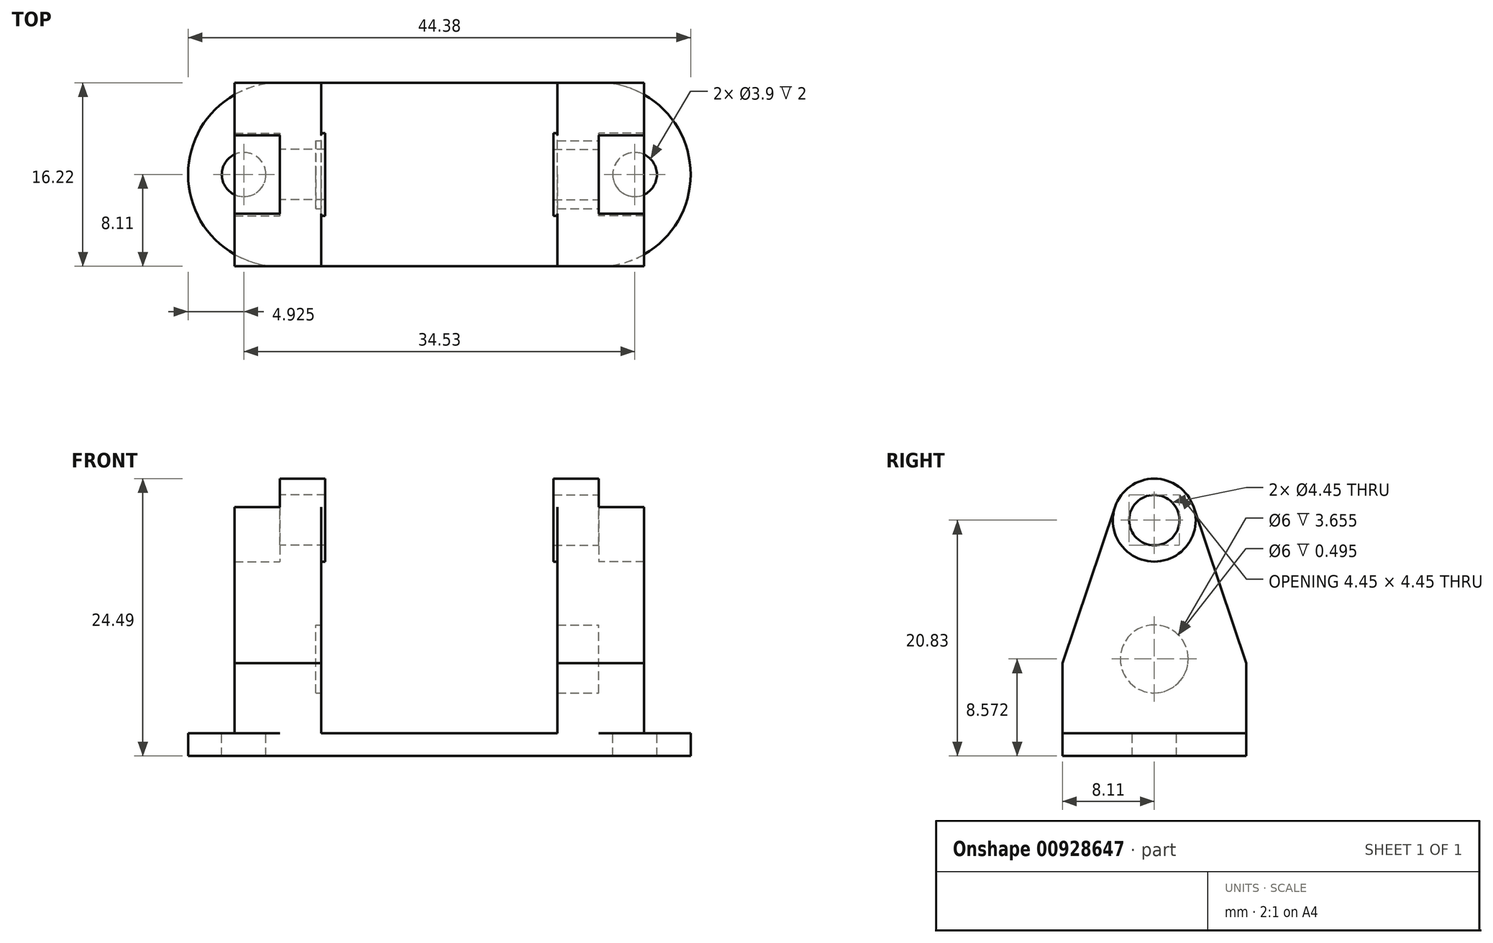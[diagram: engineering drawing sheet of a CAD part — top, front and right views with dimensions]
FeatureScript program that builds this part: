
annotation { "Feature Type Name" : "Feature", "Feature Type Description" : "" }
export const myFeature = defineFeature(function(context is Context, id is Id, definition is map)
    precondition{}
    {
        {
            var Q0;
            Q0=qCreatedBy(makeId("Top.planeOp"),FACE);
            var sketch = newSketch(context, id + "F0", { "sketchPlane" : qUnion([Q0])});
            skLineSegment(sketch, "E0.bottom", {"start": v(0, -8.1) * mm, "end": v(-14.08, -8.11) * mm});
            skLineSegment(sketch, "E0.top", {"start": v(0, 8.11) * mm, "end": v(-14.08, 8.1) * mm});
            skPoint(sketch, "E0.middle", {"position": v(0, 0) * mm});
            skPoint(sketch, "E1.center.orphan", {"position": v(-14.08, 0) * mm});
            skArc(sketch, "E2", {"start": v(-14.08, -8.11) * mm, "mid": v(-22.2, 0) * mm, "end": v(-14.08, 8.1) * mm});
            skLineSegment(sketch, "E3", {"start": v(0, 0) * mm, "end": v(0, -8.1) * mm});
            skLineSegment(sketch, "E4", {"start": v(0, -8.1) * mm, "end": v(0, 8.1) * mm});
            skPoint(sketch, "E5.center.orphan", {"position": v(14.08, 0) * mm});
            skPoint(sketch, "E5.end.orphan", {"position": v(14.08, -8.1) * mm});
            skPoint(sketch, "E6.orphan", {"position": v(14.08, 8.11) * mm});
            skSolve(sketch);
        }
        {
            var Q0;
            Q0=makeQuery(id+"F0.imprint","IMPRINT",FACE,{"disambiguationData":[TD([[makeQuery(id+"F0.imprint","IMPRINT",EDGE,{"derivedFrom":sQuery(id+"F0.wireOp",EDGE,"E0.bottom")}),-1.0]])]});
            extrude(context, id + "F1", {"entities" : qUnion([Q0]), "depth" : 2 * mm, "offsetDistance" : 25 * mm});
        }
        {
            var Q0;
            Q0=qCreatedBy(makeId("Right.planeOp"),FACE);
            var sketch = newSketch(context, id + "F2", { "sketchPlane" : qUnion([Q0])});
            skLineSegment(sketch, "E7", {"start": v(-8.11, 2) * mm, "end": v(-8.11, 8.21) * mm});
            skLineSegment(sketch, "E8", {"start": v(-8.11, 8.21) * mm, "end": v(-3.47, 22) * mm});
            skLineSegment(sketch, "E9", {"start": v(3.47, 22) * mm, "end": v(8.1, 8.21) * mm});
            skLineSegment(sketch, "E10", {"start": v(8.1, 8.21) * mm, "end": v(8.1, 2) * mm});
            skLineSegment(sketch, "E11", {"start": v(8.1, 2) * mm, "end": v(-8.1, 2) * mm});
            skPoint(sketch, "E12.end.orphan", {"position": v(0, 20.83) * mm});
            skPoint(sketch, "E12.start.orphan", {"position": v(0, 2) * mm});
            skArc(sketch, "E13", {"start": v(3.47, 22) * mm, "mid": v(0, 24.5) * mm, "end": v(-3.47, 22) * mm});
            skSolve(sketch);
        }
        {
            var Q0;
            Q0=makeQuery(id+"F2.imprint","IMPRINT",FACE,{"disambiguationData":[TD([[makeQuery(id+"F2.imprint","IMPRINT",EDGE,{"derivedFrom":sQuery(id+"F2.wireOp",EDGE,"E7")}),-1.0]])]});
            extrude(context, id + "F3", {"entities" : qUnion([Q0]), "operationType" : NewBodyOperationType.ADD, "oppositeDirection" : true, "depth" : 14.08 * mm, "offsetDistance" : 25 * mm});
        }
        {
            var Q0;
            Q0=makeQuery(id+"F3.opExtrude","CAP_FACE",FACE,{"disambiguationData":[OSD([sQuery(id+"F2.wireOp",EDGE,"E7"),sQuery(id+"F2.wireOp",EDGE,"E8"),sQuery(id+"F2.wireOp",EDGE,"284b882a-70f0-48d0-840a-5051115d6a00"),sQuery(id+"F2.wireOp",EDGE,"E9"),sQuery(id+"F2.wireOp",EDGE,"E10"),sQuery(id+"F2.wireOp",EDGE,"E11")])],"isStart":true});
            extrude(context, id + "F4", {"entities" : qUnion([Q0]), "operationType" : NewBodyOperationType.REMOVE, "oppositeDirection" : true, "depth" : 10.43 * mm, "offsetDistance" : 25 * mm});
        }
        {
            var Q0;
            Q0=makeQuery(id+"F3.opExtrude","CAP_FACE",FACE,{"disambiguationData":[OSD([sQuery(id+"F2.wireOp",EDGE,"E7"),sQuery(id+"F2.wireOp",EDGE,"E8"),sQuery(id+"F2.wireOp",EDGE,"E9"),sQuery(id+"F2.wireOp",EDGE,"E10"),sQuery(id+"F2.wireOp",EDGE,"E11"),sQuery(id+"F2.wireOp",EDGE,"E13")])],"isStart":false});
            var sketch = newSketch(context, id + "F5", { "sketchPlane" : qUnion([Q0])});
            skCircle(sketch, "E14", {"center": v(0, 20.83) * mm, "radius": 3.66 * mm});
            skSolve(sketch);
        }
        {
            var Q0;
            {var subQ0=sQuery(id+"F5.wireOp",EDGE,"E14");Q0=makeQuery(id+"F5.imprint","IMPRINT",FACE,{"disambiguationData":[TD([[makeQuery(id+"F5.imprint","IMPRINT",EDGE,{"disambiguationData":[OD(0.0)],"derivedFrom":subQ0}),-1.0]])]});}
            extrude(context, id + "F6", {"entities" : qUnion([Q0]), "operationType" : NewBodyOperationType.ADD, "depth" : 4 * mm, "offsetDistance" : 25 * mm});
        }
        {
            var Q0;
            Q0=makeQuery(id+"F4.boolean.opBoolean","COPY",FACE,{"derivedFrom":makeQuery(id+"F4.opExtrude","CAP_FACE",FACE,{"disambiguationData":[OSD([sQuery(id+"F2.wireOp",EDGE,"E7"),sQuery(id+"F2.wireOp",EDGE,"E8"),sQuery(id+"F2.wireOp",EDGE,"E9"),sQuery(id+"F2.wireOp",EDGE,"E10"),sQuery(id+"F2.wireOp",EDGE,"E11"),sQuery(id+"F2.wireOp",EDGE,"E13")])],"isStart":false})});
            var sketch = newSketch(context, id + "F7", { "sketchPlane" : qUnion([Q0])});
            skCircle(sketch, "E15", {"center": v(0, 20.83) * mm, "radius": 3.66 * mm});
            skSolve(sketch);
        }
        {
            var Q0;
            {var subQ0=sQuery(id+"F7.wireOp",EDGE,"E15");var subQ1=makeQuery(id+"F7.imprint","INTERSECT",VERTEX,{"derivedFrom":[makeQuery(id+"F4.boolean.opBoolean","COPY",EDGE,{"derivedFrom":makeQuery(id+"F4.opExtrude","CAP_EDGE",EDGE,{"disambiguationData":[OSD([sQuery(id+"F2.wireOp",EDGE,"E8")])],"isStart":false})}),subQ0]});Q0=makeQuery(id+"F7.imprint","IMPRINT",FACE,{"disambiguationData":[TD([[makeQuery(id+"F7.imprint","IMPRINT",EDGE,{"disambiguationData":[TD([[subQ1,1.0]])],"derivedFrom":subQ0}),1.0]])]});}
            extrude(context, id + "F8", {"entities" : qUnion([Q0]), "operationType" : NewBodyOperationType.ADD, "depth" : 0.34 * mm, "offsetDistance" : 25 * mm});
        }
        {
            var Q0;
            Q0=makeQuery(id+"F6.opExtrude","CAP_FACE",FACE,{"disambiguationData":[OSD([sQuery(id+"F5.wireOp",EDGE,"E14")])],"isStart":false});
            var sketch = newSketch(context, id + "F9", { "sketchPlane" : qUnion([Q0])});
            skCircle(sketch, "E16", {"center": v(0, 20.83) * mm, "radius": 2.23 * mm});
            skSolve(sketch);
        }
        {
            var Q0;
            Q0=makeQuery(id+"F9.imprint","IMPRINT",FACE,{"disambiguationData":[TD([[makeQuery(id+"F9.imprint","IMPRINT",EDGE,{"derivedFrom":sQuery(id+"F9.wireOp",EDGE,"E16")}),1.0]])]});
            var Q1;
            Q1=sQuery(id+"F9.wireOp",EDGE,"E16");
            extrude(context, id + "F10", {"entities" : qUnion([Q0]), "operationType" : NewBodyOperationType.REMOVE, "surfaceEntities" : qUnion([Q1]), "oppositeDirection" : true, "depth" : 8 * mm, "offsetDistance" : 25 * mm});
        }
        {
            var Q0;
            {var subQ1=sQuery(id+"F0.wireOp",EDGE,"E0.top");var subQ3=sQuery(id+"F0.wireOp",EDGE,"E2");var subQ4=sQuery(id+"F0.wireOp",EDGE,"E0.bottom");Q0=makeQuery(id+"F3.boolean.opBoolean","SPLIT",FACE,{"disambiguationData":[TD([makeQuery(id+"F1.opExtrude","SWEPT_FACE",FACE,{"disambiguationData":[OSD([subQ3])]})])],"derivedFrom":makeQuery(id+"F1.opExtrude","CAP_FACE",FACE,{"disambiguationData":[OSD([subQ4,subQ1,sQuery(id+"F0.wireOp",EDGE,"E5"),subQ3])],"isStart":false})});}
            var sketch = newSketch(context, id + "F11", { "sketchPlane" : qUnion([Q0])});
            skCircle(sketch, "E17", {"center": v(-17.27, 0) * mm, "radius": 1.95 * mm});
            skSolve(sketch);
        }
        {
            var Q0;
            Q0=makeQuery(id+"F11.imprint","IMPRINT",FACE,{"disambiguationData":[TD([[makeQuery(id+"F11.imprint","IMPRINT",EDGE,{"derivedFrom":sQuery(id+"F11.wireOp",EDGE,"E17")}),1.0]])]});
            extrude(context, id + "F12", {"entities" : qUnion([Q0]), "operationType" : NewBodyOperationType.REMOVE, "oppositeDirection" : true, "depth" : 2 * mm, "offsetDistance" : 25 * mm});
        }
        {
            var Q0;
            Q0 = qSketchRegion(id + "F0", true);
            var sketch = newSketch(context, id + "F13", { "sketchPlane" : qUnion([Q0])});
            skLineSegment(sketch, "E18.bottom", {"start": v(-10.43, -8.1) * mm, "end": v(0, -8.1) * mm});
            skLineSegment(sketch, "E18.top", {"start": v(-10.43, 8.11) * mm, "end": v(0, 8.11) * mm});
            skLineSegment(sketch, "E18.left", {"start": v(-10.43, -8.1) * mm, "end": v(-10.43, 8.11) * mm});
            skLineSegment(sketch, "E18.right", {"start": v(0, -8.1) * mm, "end": v(0, 8.11) * mm});
            skSolve(sketch);
        }
        {
            var Q0;
            Q0=makeQuery(id+"F13.imprint","IMPRINT",FACE,{"disambiguationData":[TD([[makeQuery(id+"F13.imprint","IMPRINT",EDGE,{"derivedFrom":sQuery(id+"F13.wireOp",EDGE,"E18.bottom")}),-1.0]])]});
            extrude(context, id + "F14", {"entities" : qUnion([Q0]), "operationType" : NewBodyOperationType.ADD, "depth" : 2 * mm, "offsetDistance" : 25 * mm});
        }
        {
            var Q0;
            Q0=makeQuery(id+"F1.opExtrude","SWEPT_BODY",BODY,{"disambiguationData":[OSD([sQuery(id+"F0.wireOp",EDGE,"E0.bottom"),sQuery(id+"F0.wireOp",EDGE,"E0.top"),sQuery(id+"F0.wireOp",EDGE,"E2"),sQuery(id+"F0.wireOp",EDGE,"E4")])]});
            var Q1;
            Q1=qCreatedBy(makeId("Right.planeOp"),FACE);
            mirror(context, id + "F15", {"operationType" : NewBodyOperationType.ADD, "entities" : qUnion([Q0]), "mirrorPlane" : qUnion([Q1])});
        }
        {
            var Q0;
            Q0=makeQuery(id+"F15.opPattern","COPY",FACE,{"derivedFrom":makeQuery(id+"F3.opExtrude","CAP_FACE",FACE,{"disambiguationData":[OSD([sQuery(id+"F2.wireOp",EDGE,"E7"),sQuery(id+"F2.wireOp",EDGE,"E8"),sQuery(id+"F2.wireOp",EDGE,"E9"),sQuery(id+"F2.wireOp",EDGE,"E10"),sQuery(id+"F2.wireOp",EDGE,"E11"),sQuery(id+"F2.wireOp",EDGE,"E13")])],"isStart":false}),"instanceName":"1"});
            var sketch = newSketch(context, id + "F16", { "sketchPlane" : qUnion([Q0])});
            skCircle(sketch, "E19", {"center": v(0, 8.57) * mm, "radius": 3 * mm});
            skSolve(sketch);
        }
        {
            var Q0;
            Q0=makeQuery(id+"F16.imprint","IMPRINT",FACE,{"disambiguationData":[TD([[makeQuery(id+"F16.imprint","IMPRINT",EDGE,{"derivedFrom":sQuery(id+"F16.wireOp",EDGE,"E19")}),1.0]])]});
            extrude(context, id + "F17", {"entities" : qUnion([Q0]), "operationType" : NewBodyOperationType.REMOVE, "oppositeDirection" : true, "depth" : 25 * mm, "offsetDistance" : 25 * mm});
        }
    });
